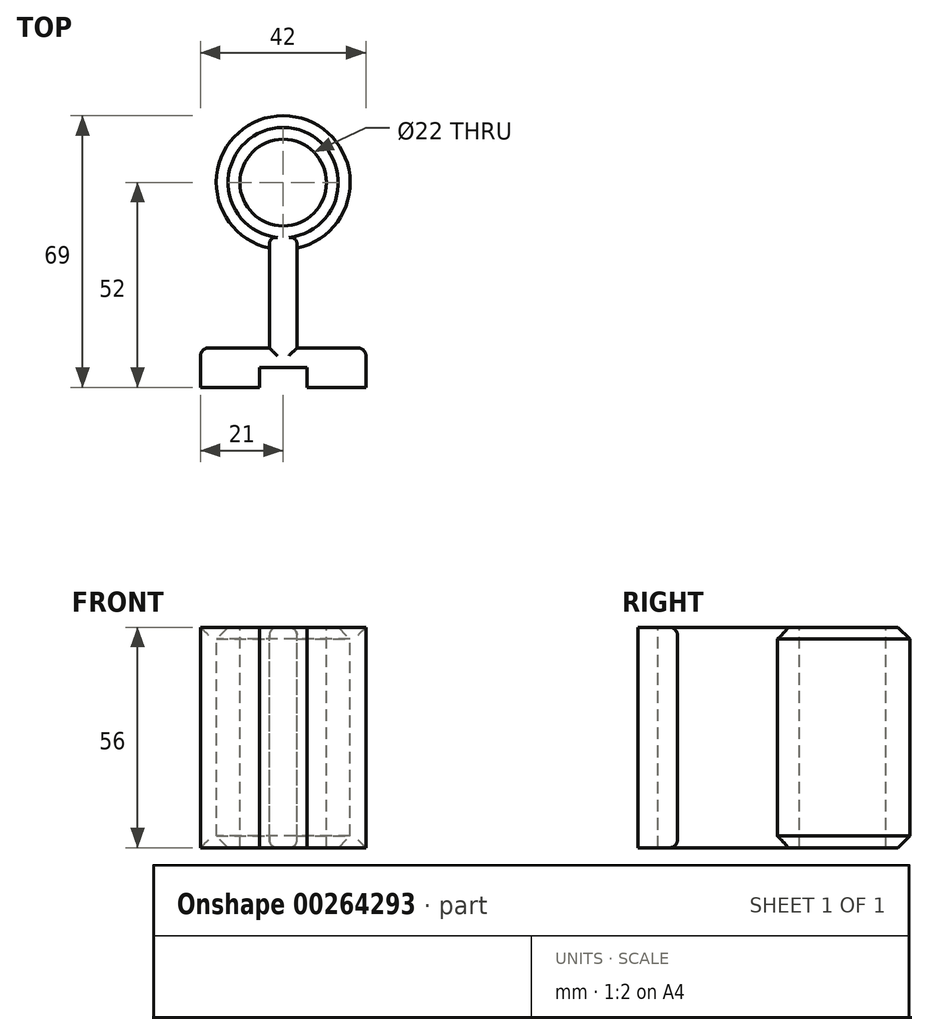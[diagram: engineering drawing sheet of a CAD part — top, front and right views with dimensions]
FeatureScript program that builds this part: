
annotation { "Feature Type Name" : "Feature", "Feature Type Description" : "" }
export const myFeature = defineFeature(function(context is Context, id is Id, definition is map)
    precondition{}
    {
        {
            var Q0;
            Q0=qCreatedBy(makeId("Top.planeOp"),FACE);
            var sketch = newSketch(context, id + "F0", { "sketchPlane" : qUnion([Q0])});
            skLineSegment(sketch, "E0", {"start": v(0, 0) * mm, "end": v(0, 25.36) * mm});
            skLineSegment(sketch, "E1", {"start": v(0, 0) * mm, "end": v(-17.5, 0) * mm});
            skLineSegment(sketch, "E2", {"start": v(-17.5, 0) * mm, "end": v(-17.5, -10) * mm});
            skLineSegment(sketch, "E3", {"start": v(-17.5, -10) * mm, "end": v(-2.5, -10) * mm});
            skLineSegment(sketch, "E4", {"start": v(-2.5, -10) * mm, "end": v(-2.5, -5) * mm});
            skLineSegment(sketch, "E5", {"start": v(-2.5, -5) * mm, "end": v(9.5, -5) * mm});
            skLineSegment(sketch, "E6", {"start": v(9.5, -5) * mm, "end": v(9.5, -10) * mm});
            skLineSegment(sketch, "E7", {"start": v(9.5, -10) * mm, "end": v(24.5, -10) * mm});
            skLineSegment(sketch, "E8", {"start": v(24.5, -10) * mm, "end": v(24.5, 0) * mm});
            skLineSegment(sketch, "E9", {"start": v(24.5, 0) * mm, "end": v(7, 0) * mm});
            skLineSegment(sketch, "E10", {"start": v(7, 0) * mm, "end": v(7, 25.36) * mm});
            skCircle(sketch, "E11", {"center": v(3.5, 42) * mm, "radius": 11 * mm});
            skArc(sketch, "E12", {"start": v(7, 25.36) * mm, "mid": v(3.5, 59) * mm, "end": v(0, 25.36) * mm});
            skSolve(sketch);
        }
        {
            var Q0;
            Q0=makeQuery(id+"F0.imprint","IMPRINT",FACE,{"disambiguationData":[TD([[makeQuery(id+"F0.imprint","IMPRINT",EDGE,{"derivedFrom":sQuery(id+"F0.wireOp",EDGE,"E0")}),-1.0]])]});
            extrude(context, id + "F1", {"entities" : qUnion([Q0]), "oppositeDirection" : true, "depth" : 56 * mm});
        }
        {
            var Q0;
            Q0=makeQuery(id+"F1.opExtrude","CAP_EDGE",EDGE,{"disambiguationData":[OSD([sQuery(id+"F0.wireOp",EDGE,"E0")])],"isStart":false});
            var Q1;
            Q1=makeQuery(id+"F1.opExtrude","CAP_EDGE",EDGE,{"disambiguationData":[OSD([sQuery(id+"F0.wireOp",EDGE,"E1")])],"isStart":false});
            var Q2;
            Q2=makeQuery(id+"F1.opExtrude","SWEPT_EDGE",EDGE,{"disambiguationData":[OSD([sQuery(id+"F0.wireOp",EDGE,"E1"),sQuery(id+"F0.wireOp",EDGE,"E2")])]});
            var Q3;
            Q3=makeQuery(id+"F1.opExtrude","CAP_EDGE",EDGE,{"disambiguationData":[OSD([sQuery(id+"F0.wireOp",EDGE,"E0")])],"isStart":true});
            var Q4;
            Q4=makeQuery(id+"F1.opExtrude","CAP_EDGE",EDGE,{"disambiguationData":[OSD([sQuery(id+"F0.wireOp",EDGE,"E1")])],"isStart":true});
            fillet(context, id + "F2", {"entities" : qUnion([Q0, Q1, Q2, Q3, Q4]), "radius" : 2 * mm, "allowEdgeOverflow" : false});
        }
        {
            var Q0;
            Q0=makeQuery(id+"F1.opExtrude","CAP_EDGE",EDGE,{"disambiguationData":[OSD([sQuery(id+"F0.wireOp",EDGE,"E9")])],"isStart":false});
            var Q1;
            Q1=makeQuery(id+"F1.opExtrude","SWEPT_EDGE",EDGE,{"disambiguationData":[OSD([sQuery(id+"F0.wireOp",EDGE,"E8"),sQuery(id+"F0.wireOp",EDGE,"E9")])]});
            var Q2;
            Q2=makeQuery(id+"F1.opExtrude","CAP_EDGE",EDGE,{"disambiguationData":[OSD([sQuery(id+"F0.wireOp",EDGE,"E9")])],"isStart":true});
            var Q3;
            Q3=makeQuery(id+"F1.opExtrude","CAP_EDGE",EDGE,{"disambiguationData":[OSD([sQuery(id+"F0.wireOp",EDGE,"E10")])],"isStart":true});
            var Q4;
            Q4=makeQuery(id+"F1.opExtrude","CAP_EDGE",EDGE,{"disambiguationData":[OSD([sQuery(id+"F0.wireOp",EDGE,"E10")])],"isStart":false});
            fillet(context, id + "F3", {"entities" : qUnion([Q0, Q1, Q2, Q3, Q4]), "radius" : 2 * mm, "tangentPropagation" : true, "allowEdgeOverflow" : false});
        }
        {
            var Q0;
            Q0=makeQuery(id+"F1.opExtrude","CAP_EDGE",EDGE,{"disambiguationData":[OSD([sQuery(id+"F0.wireOp",EDGE,"E12")])],"isStart":true});
            var Q1;
            Q1=makeQuery(id+"F1.opExtrude","CAP_EDGE",EDGE,{"disambiguationData":[OSD([sQuery(id+"F0.wireOp",EDGE,"E12")])],"isStart":false});
            chamfer(context, id + "F4", {"entities" : qUnion([Q0, Q1]), "width" : 3 * mm, "tangentPropagation" : true});
        }
    });
